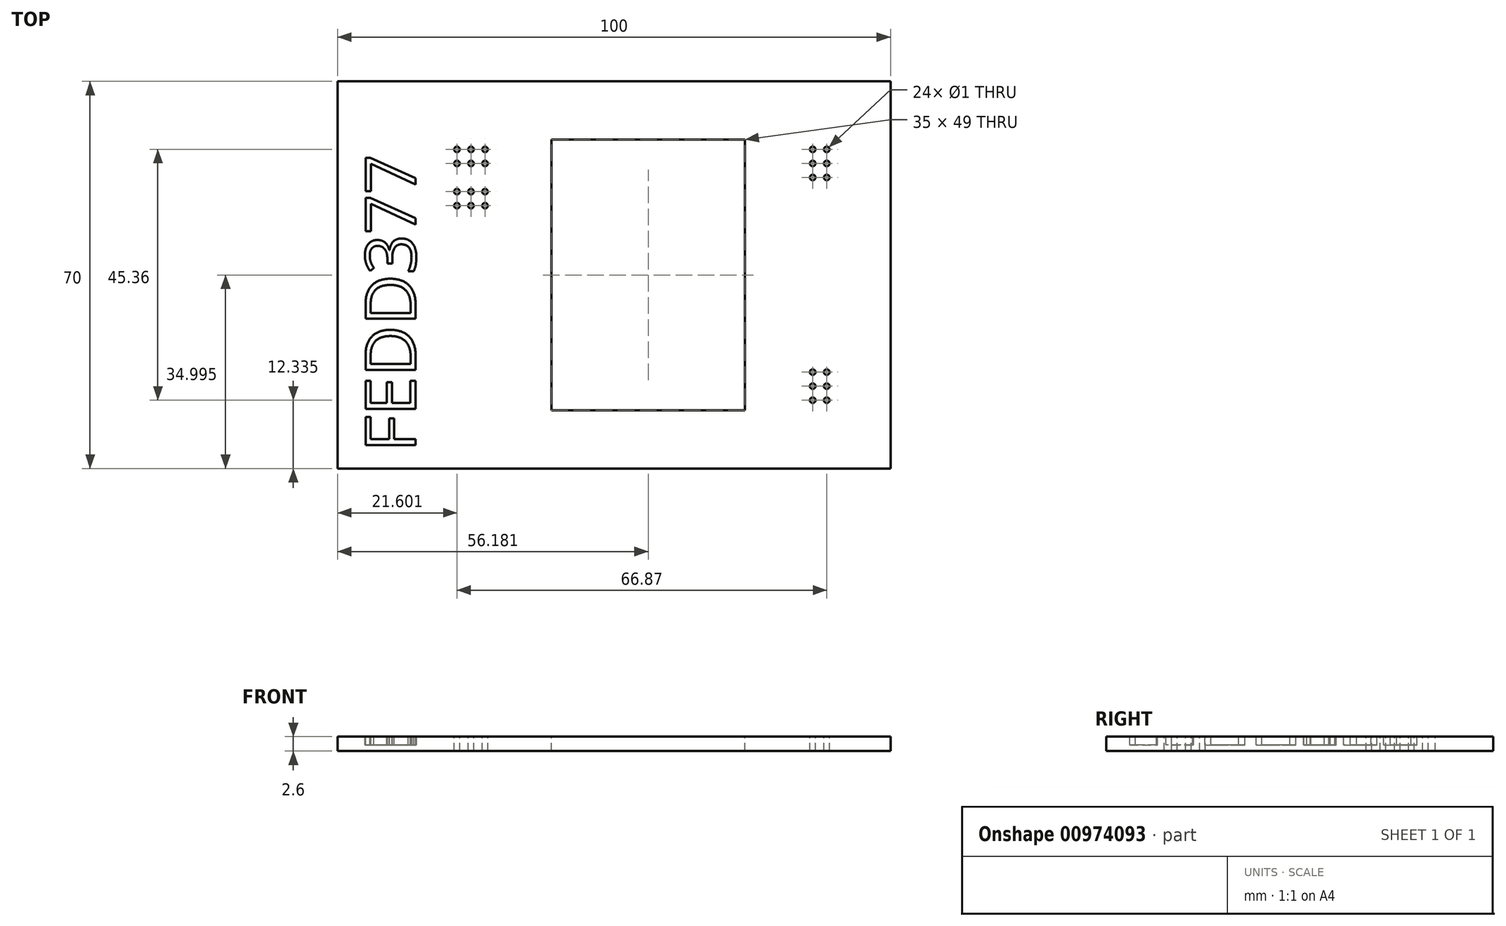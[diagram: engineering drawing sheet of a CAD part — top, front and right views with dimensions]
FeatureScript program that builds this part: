
annotation { "Feature Type Name" : "Feature", "Feature Type Description" : "" }
export const myFeature = defineFeature(function(context is Context, id is Id, definition is map)
    precondition{}
    {
        {
            var Q0;
            Q0=qCreatedBy(makeId("Top.planeOp"),FACE);
            var sketch = newSketch(context, id + "F0", { "sketchPlane" : qUnion([Q0])});
            skLineSegment(sketch, "E0.bottom", {"start": v(-43.16, 48.34) * mm, "end": v(56.84, 48.34) * mm});
            skLineSegment(sketch, "E0.top", {"start": v(-43.16, -21.66) * mm, "end": v(56.84, -21.66) * mm});
            skLineSegment(sketch, "E0.left", {"start": v(-43.16, 48.34) * mm, "end": v(-43.16, -21.66) * mm});
            skLineSegment(sketch, "E0.right", {"start": v(56.84, 48.34) * mm, "end": v(56.84, -21.66) * mm});
            skSolve(sketch);
        }
        {
            var Q0;
            Q0=makeQuery(id+"F0.imprint","IMPRINT",FACE,{"disambiguationData":[TD([[makeQuery(id+"F0.imprint","IMPRINT",EDGE,{"derivedFrom":sQuery(id+"F0.wireOp",EDGE,"E0.bottom")}),-1.0]])]});
            extrude(context, id + "F1", {"entities" : qUnion([Q0]), "depth" : 2.6 * mm, "offsetDistance" : 25 * mm});
        }
        {
            var Q0;
            Q0=makeQuery(id+"F1.opExtrude","CAP_FACE",FACE,{"disambiguationData":[OSD([sQuery(id+"F0.wireOp",EDGE,"E0.bottom"),sQuery(id+"F0.wireOp",EDGE,"E0.top"),sQuery(id+"F0.wireOp",EDGE,"E0.left"),sQuery(id+"F0.wireOp",EDGE,"E0.right")])],"isStart":false});
            var sketch = newSketch(context, id + "F2", { "sketchPlane" : qUnion([Q0])});
            skText(sketch, "E1", { "text": "FEDD377", "fontName": "OpenSans-Regular.ttf"});
            const initialGuessF2  = {"E1": [-0.02903, -0.01866, 0, 1, 0.00913]};
            skSetInitialGuess(sketch, initialGuessF2);
            skSolve(sketch);
        }
        {
            var Q0;
            Q0=qSketchRegion(id+"F2",true);
            extrude(context, id + "F3", {"entities" : qUnion([Q0]), "operationType" : NewBodyOperationType.REMOVE, "oppositeDirection" : true, "depth" : 1.5 * mm, "offsetDistance" : 25 * mm});
        }
        {
            var Q0;
            {var subQ0=sQuery(id+"F0.wireOp",EDGE,"E0.left");var subQ1=sQuery(id+"F0.wireOp",EDGE,"E0.bottom");var subQ2=sQuery(id+"F0.wireOp",EDGE,"E0.right");var subQ3=sQuery(id+"F0.wireOp",EDGE,"E0.top");Q0=makeQuery(id+"F3.boolean.opBoolean","SPLIT",FACE,{"disambiguationData":[TD([makeQuery(id+"F1.opExtrude","SWEPT_FACE",FACE,{"disambiguationData":[OSD([subQ1])]})])],"derivedFrom":makeQuery(id+"F1.opExtrude","CAP_FACE",FACE,{"disambiguationData":[OSD([subQ1,subQ3,subQ0,subQ2])],"isStart":false})});}
            var sketch = newSketch(context, id + "F4", { "sketchPlane" : qUnion([Q0])});
            skLineSegment(sketch, "E2.bottom", {"start": v(-23.16, 37.84) * mm, "end": v(56.84, 37.84) * mm});
            skLineSegment(sketch, "E2.top", {"start": v(-23.16, -11.16) * mm, "end": v(56.84, -11.16) * mm});
            skLineSegment(sketch, "E2.left", {"start": v(-23.16, 37.84) * mm, "end": v(-23.16, -11.16) * mm});
            skLineSegment(sketch, "E2.right", {"start": v(56.84, 37.84) * mm, "end": v(56.84, -11.16) * mm});
            skCircle(sketch, "E3", {"center": v(42.77, -9.32) * mm, "radius": 0.5 * mm});
            skCircle(sketch, "E4", {"center": v(42.77, -6.78) * mm, "radius": 0.5 * mm});
            skCircle(sketch, "E5", {"center": v(42.77, -4.24) * mm, "radius": 0.5 * mm});
            skCircle(sketch, "E6", {"center": v(45.31, -4.24) * mm, "radius": 0.5 * mm});
            skCircle(sketch, "E7", {"center": v(45.31, -6.78) * mm, "radius": 0.5 * mm});
            skCircle(sketch, "E8", {"center": v(45.31, -9.32) * mm, "radius": 0.5 * mm});
            skCircle(sketch, "E9", {"center": v(42.77, 30.96) * mm, "radius": 0.5 * mm});
            skCircle(sketch, "E10", {"center": v(42.77, 33.5) * mm, "radius": 0.5 * mm});
            skCircle(sketch, "E11", {"center": v(42.77, 36.04) * mm, "radius": 0.5 * mm});
            skCircle(sketch, "E12", {"center": v(45.31, 36.04) * mm, "radius": 0.5 * mm});
            skCircle(sketch, "E13", {"center": v(45.31, 33.5) * mm, "radius": 0.5 * mm});
            skCircle(sketch, "E14", {"center": v(45.31, 30.96) * mm, "radius": 0.5 * mm});
            skCircle(sketch, "E15", {"center": v(-16.48, 25.86) * mm, "radius": 0.5 * mm});
            skCircle(sketch, "E16", {"center": v(-19.02, 25.86) * mm, "radius": 0.5 * mm});
            skCircle(sketch, "E17", {"center": v(-21.56, 25.86) * mm, "radius": 0.5 * mm});
            skCircle(sketch, "E18", {"center": v(-21.56, 28.4) * mm, "radius": 0.5 * mm});
            skCircle(sketch, "E19", {"center": v(-19.02, 28.4) * mm, "radius": 0.5 * mm});
            skCircle(sketch, "E20", {"center": v(-16.48, 28.4) * mm, "radius": 0.5 * mm});
            skCircle(sketch, "E21", {"center": v(-16.48, 33.5) * mm, "radius": 0.5 * mm});
            skCircle(sketch, "E22", {"center": v(-19.02, 33.5) * mm, "radius": 0.5 * mm});
            skCircle(sketch, "E23", {"center": v(-21.56, 33.5) * mm, "radius": 0.5 * mm});
            skCircle(sketch, "E24", {"center": v(-21.56, 36.04) * mm, "radius": 0.5 * mm});
            skCircle(sketch, "E25", {"center": v(-19.02, 36.04) * mm, "radius": 0.5 * mm});
            skCircle(sketch, "E26", {"center": v(-16.48, 36.04) * mm, "radius": 0.5 * mm});
            skLineSegment(sketch, "E27", {"start": v(-4.48, 37.84) * mm, "end": v(-4.48, -11.16) * mm});
            skLineSegment(sketch, "E28", {"start": v(30.52, 37.84) * mm, "end": v(30.52, -11.16) * mm});
            skSolve(sketch);
        }
        {
            var Q0;
            {var subQ0=sQuery(id+"F4.wireOp",EDGE,"E27");Q0=makeQuery(id+"F4.imprint","IMPRINT",FACE,{"disambiguationData":[TD([[makeQuery(id+"F4.imprint","IMPRINT",EDGE,{"derivedFrom":subQ0}),1.0]])]});}
            var Q1;
            Q1=makeQuery(id+"F4.imprint","IMPRINT",FACE,{"disambiguationData":[TD([[makeQuery(id+"F4.imprint","IMPRINT",EDGE,{"derivedFrom":sQuery(id+"F4.wireOp",EDGE,"E24")}),1.0]])]});
            var Q2;
            Q2=makeQuery(id+"F4.imprint","IMPRINT",FACE,{"disambiguationData":[TD([[makeQuery(id+"F4.imprint","IMPRINT",EDGE,{"derivedFrom":sQuery(id+"F4.wireOp",EDGE,"E25")}),1.0]])]});
            var Q3;
            Q3=makeQuery(id+"F4.imprint","IMPRINT",FACE,{"disambiguationData":[TD([[makeQuery(id+"F4.imprint","IMPRINT",EDGE,{"derivedFrom":sQuery(id+"F4.wireOp",EDGE,"E26")}),1.0]])]});
            var Q4;
            Q4=makeQuery(id+"F4.imprint","IMPRINT",FACE,{"disambiguationData":[TD([[makeQuery(id+"F4.imprint","IMPRINT",EDGE,{"derivedFrom":sQuery(id+"F4.wireOp",EDGE,"E21")}),1.0]])]});
            var Q5;
            Q5=makeQuery(id+"F4.imprint","IMPRINT",FACE,{"disambiguationData":[TD([[makeQuery(id+"F4.imprint","IMPRINT",EDGE,{"derivedFrom":sQuery(id+"F4.wireOp",EDGE,"E20")}),1.0]])]});
            var Q6;
            Q6=makeQuery(id+"F4.imprint","IMPRINT",FACE,{"disambiguationData":[TD([[makeQuery(id+"F4.imprint","IMPRINT",EDGE,{"derivedFrom":sQuery(id+"F4.wireOp",EDGE,"E15")}),1.0]])]});
            var Q7;
            Q7=makeQuery(id+"F4.imprint","IMPRINT",FACE,{"disambiguationData":[TD([[makeQuery(id+"F4.imprint","IMPRINT",EDGE,{"derivedFrom":sQuery(id+"F4.wireOp",EDGE,"E16")}),1.0]])]});
            var Q8;
            Q8=makeQuery(id+"F4.imprint","IMPRINT",FACE,{"disambiguationData":[TD([[makeQuery(id+"F4.imprint","IMPRINT",EDGE,{"derivedFrom":sQuery(id+"F4.wireOp",EDGE,"E17")}),1.0]])]});
            var Q9;
            Q9=makeQuery(id+"F4.imprint","IMPRINT",FACE,{"disambiguationData":[TD([[makeQuery(id+"F4.imprint","IMPRINT",EDGE,{"derivedFrom":sQuery(id+"F4.wireOp",EDGE,"E18")}),1.0]])]});
            var Q10;
            Q10=makeQuery(id+"F4.imprint","IMPRINT",FACE,{"disambiguationData":[TD([[makeQuery(id+"F4.imprint","IMPRINT",EDGE,{"derivedFrom":sQuery(id+"F4.wireOp",EDGE,"E19")}),1.0]])]});
            var Q11;
            Q11=makeQuery(id+"F4.imprint","IMPRINT",FACE,{"disambiguationData":[TD([[makeQuery(id+"F4.imprint","IMPRINT",EDGE,{"derivedFrom":sQuery(id+"F4.wireOp",EDGE,"E22")}),1.0]])]});
            var Q12;
            Q12=makeQuery(id+"F4.imprint","IMPRINT",FACE,{"disambiguationData":[TD([[makeQuery(id+"F4.imprint","IMPRINT",EDGE,{"derivedFrom":sQuery(id+"F4.wireOp",EDGE,"E23")}),1.0]])]});
            var Q13;
            Q13=makeQuery(id+"F4.imprint","IMPRINT",FACE,{"disambiguationData":[TD([[makeQuery(id+"F4.imprint","IMPRINT",EDGE,{"derivedFrom":sQuery(id+"F4.wireOp",EDGE,"E4")}),1.0]])]});
            var Q14;
            Q14=makeQuery(id+"F4.imprint","IMPRINT",FACE,{"disambiguationData":[TD([[makeQuery(id+"F4.imprint","IMPRINT",EDGE,{"derivedFrom":sQuery(id+"F4.wireOp",EDGE,"E8")}),1.0]])]});
            var Q15;
            Q15=makeQuery(id+"F4.imprint","IMPRINT",FACE,{"disambiguationData":[TD([[makeQuery(id+"F4.imprint","IMPRINT",EDGE,{"derivedFrom":sQuery(id+"F4.wireOp",EDGE,"E7")}),1.0]])]});
            var Q16;
            Q16=makeQuery(id+"F4.imprint","IMPRINT",FACE,{"disambiguationData":[TD([[makeQuery(id+"F4.imprint","IMPRINT",EDGE,{"derivedFrom":sQuery(id+"F4.wireOp",EDGE,"E3")}),1.0]])]});
            var Q17;
            Q17=makeQuery(id+"F4.imprint","IMPRINT",FACE,{"disambiguationData":[TD([[makeQuery(id+"F4.imprint","IMPRINT",EDGE,{"derivedFrom":sQuery(id+"F4.wireOp",EDGE,"E6")}),1.0]])]});
            var Q18;
            Q18=makeQuery(id+"F4.imprint","IMPRINT",FACE,{"disambiguationData":[TD([[makeQuery(id+"F4.imprint","IMPRINT",EDGE,{"derivedFrom":sQuery(id+"F4.wireOp",EDGE,"E5")}),1.0]])]});
            var Q19;
            Q19=makeQuery(id+"F4.imprint","IMPRINT",FACE,{"disambiguationData":[TD([[makeQuery(id+"F4.imprint","IMPRINT",EDGE,{"derivedFrom":sQuery(id+"F4.wireOp",EDGE,"E14")}),1.0]])]});
            var Q20;
            Q20=makeQuery(id+"F4.imprint","IMPRINT",FACE,{"disambiguationData":[TD([[makeQuery(id+"F4.imprint","IMPRINT",EDGE,{"derivedFrom":sQuery(id+"F4.wireOp",EDGE,"E9")}),1.0]])]});
            var Q21;
            Q21=makeQuery(id+"F4.imprint","IMPRINT",FACE,{"disambiguationData":[TD([[makeQuery(id+"F4.imprint","IMPRINT",EDGE,{"derivedFrom":sQuery(id+"F4.wireOp",EDGE,"E10")}),1.0]])]});
            var Q22;
            Q22=makeQuery(id+"F4.imprint","IMPRINT",FACE,{"disambiguationData":[TD([[makeQuery(id+"F4.imprint","IMPRINT",EDGE,{"derivedFrom":sQuery(id+"F4.wireOp",EDGE,"E13")}),1.0]])]});
            var Q23;
            Q23=makeQuery(id+"F4.imprint","IMPRINT",FACE,{"disambiguationData":[TD([[makeQuery(id+"F4.imprint","IMPRINT",EDGE,{"derivedFrom":sQuery(id+"F4.wireOp",EDGE,"E12")}),1.0]])]});
            var Q24;
            Q24=makeQuery(id+"F4.imprint","IMPRINT",FACE,{"disambiguationData":[TD([[makeQuery(id+"F4.imprint","IMPRINT",EDGE,{"derivedFrom":sQuery(id+"F4.wireOp",EDGE,"E11")}),1.0]])]});
            extrude(context, id + "F5", {"entities" : qUnion([Q0, Q1, Q2, Q3, Q4, Q5, Q6, Q7, Q8, Q9, Q10, Q11, Q12, Q13, Q14, Q15, Q16, Q17, Q18, Q19, Q20, Q21, Q22, Q23, Q24]), "operationType" : NewBodyOperationType.REMOVE, "endBound" : BoundingType.UP_TO_NEXT, "oppositeDirection" : true, "depth" : 25 * mm, "offsetDistance" : 25 * mm});
        }
    });
